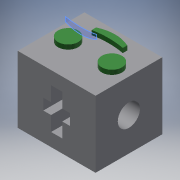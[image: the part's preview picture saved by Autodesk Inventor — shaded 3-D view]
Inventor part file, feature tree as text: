
AUTODESK INVENTOR PART (.ipt)
format: ipt  version: 2019 (Build 230136000, 136)  size: 168,448 bytes
history: native  units: mm
features: other x4, extrude x4, sketch x4, projected_geometry x2, reference x1
ambient origin geometry x8: Origin, YZ Plane, XZ Plane, XY Plane, X Axis, Y Axis, Z Axis, Center Point
bodies: Body1 (feature_tree)
feature tree (15):
  other  "ソリッド1"
  extrude  "押し出し1"  Depth=35.0mm
  extrude  "押し出し2"  Depth=30.0mm
  extrude  "押し出し3"  Depth=30.0mm TaperAngle=0.0deg
  extrude  "押し出し4"  Depth=10.0mm
  sketch  "スケッチ1"
  sketch  "スケッチ4"
  projected_geometry  "投影ループ2"
  sketch  "スケッチ5"
  reference  "参照1"
  sketch  "スケッチ6"
  projected_geometry  "投影ループ3"
  other  "<userpath>\OneDrive\デスクトップ\mini_robot\mini_robot.iam"
  other  "mini_robot.iam"
  other  "body:1"
